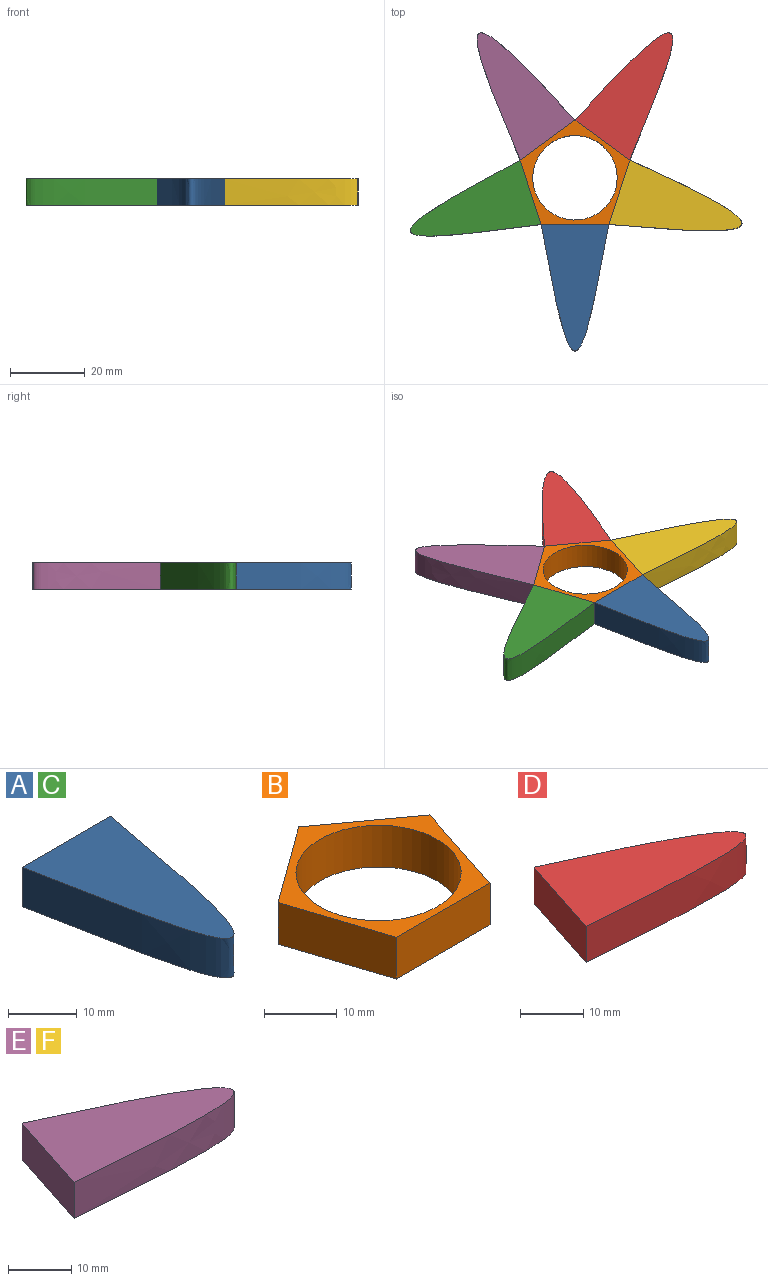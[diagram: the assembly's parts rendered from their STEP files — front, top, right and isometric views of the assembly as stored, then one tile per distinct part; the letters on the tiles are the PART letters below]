
ASSEMBLY  parts=6 mates=6
PART A: 4 faces, bbox 18.2x35.8x7 mm
  f0: plane 18.2x7mm, normal (0,1,0), area 127.4mm2, adj f1,f2,f3
  f1: extruded ~34x18.2mm, area 500mm2, adj f0,f2,f3
  f2: plane 35.8x18.2mm, normal (0,0,-1), area 382.9mm2, adj f0,f1
  f3: plane 35.8x18.2mm, normal (0,0,1), area 382.9mm2, adj f0,f1
PART B: 8 faces, bbox 29.4x28x7 mm
  f0: plane 18.2x7mm, normal (0,-1,0), area 127.4mm2, adj f1,f4,f6,f7
  f1: plane 17.31x7mm, normal (0.95,-0.31,0), area 127.4mm2, adj f0,f2,f6,f7
  f2: plane 14.72x10.7mm, normal (0.59,0.81,0), area 127.4mm2, adj f1,f3,f6,f7
  f3: plane 14.72x10.7mm, normal (-0.59,0.81,0), area 127.4mm2, adj f2,f4,f6,f7
  f4: plane 17.31x7mm, normal (-0.95,-0.31,0), area 127.4mm2, adj f0,f3,f6,f7
  f5: cylinder r=11.33mm len=22.67mm, axis (0,0,-1), area 498.5mm2, adj f6,f7
  f6: plane 29.44x28mm, normal (0,0,1), area 166.1mm2, adj f0,f1,f2,f3,f4,f5
  f7: plane 29.44x28mm, normal (0,0,-1), area 166.1mm2, adj f0,f1,f2,f3,f4,f5
PART C: same geometry as A
PART D: 4 faces, bbox 37.4x20.6x7 mm
  f0: plane 17.31x7mm, normal (-0.95,0.31,0), area 127.4mm2, adj f1,f2,f3
  f1: extruded ~35.72x18.93mm, area 500.4mm2, adj f0,f2,f3
  f2: plane 37.41x20.61mm, normal (0,0,-1), area 387.6mm2, adj f0,f1
  f3: plane 37.41x20.61mm, normal (0,0,1), area 387.6mm2, adj f0,f1
PART E: 5 faces, bbox 37.4x20.3x7 mm
  f0: extruded ~35.69x7mm, area 253.5mm2, adj f1,f2,f3,f4
  f1: extruded ~30.12x17.31mm, area 247.1mm2, adj f0,f2,f3,f4
  f2: plane 17.31x7mm, normal (-0.95,0.31,0), area 127.4mm2, adj f0,f1,f3,f4
  f3: plane 37.39x20.25mm, normal (0,0,1), area 389.6mm2, adj f0,f1,f2
  f4: plane 37.39x20.25mm, normal (0,0,-1), area 389.6mm2, adj f0,f1,f2
PART F: same geometry as E
PLACE A t=(-3.48,0.99,3.22)mm
PLACE B t=(-3.48,0.99,3.22)mm
PLACE C rot(axis=(0,0,-1),72deg) t=(-3.48,0.99,3.22)mm
PLACE D rot(axis=(0,0,1),72deg) t=(-3.48,0.99,3.22)mm
PLACE E rot(axis=(-0.59,-0.81,0),180deg) t=(-3.48,0.99,17.22)mm
PLACE F t=(-3.48,0.99,-3.78)mm
MATE parallel C.f0 <-> B.f4  axis (0.95,0.31,0) through (-15.39,-2.87,6.72)mm
MATE parallel A.f0 <-> B.f0  axis (0,1,0) through (-3.48,-11.53,6.72)mm
MATE parallel D.f0 <-> B.f2  axis (-0.59,-0.81,0) through (3.88,11.13,6.72)mm
MATE parallel C.f0 <-> B.f2  axis (0.95,0.31,0) through (-15.39,-2.87,6.72)mm
MATE parallel F.f2 <-> B.f1  axis (-0.95,0.31,0) through (8.43,-2.87,6.72)mm
MATE parallel E.f2 <-> B.f3  axis (0.59,-0.81,0) through (-10.84,11.13,6.72)mm
